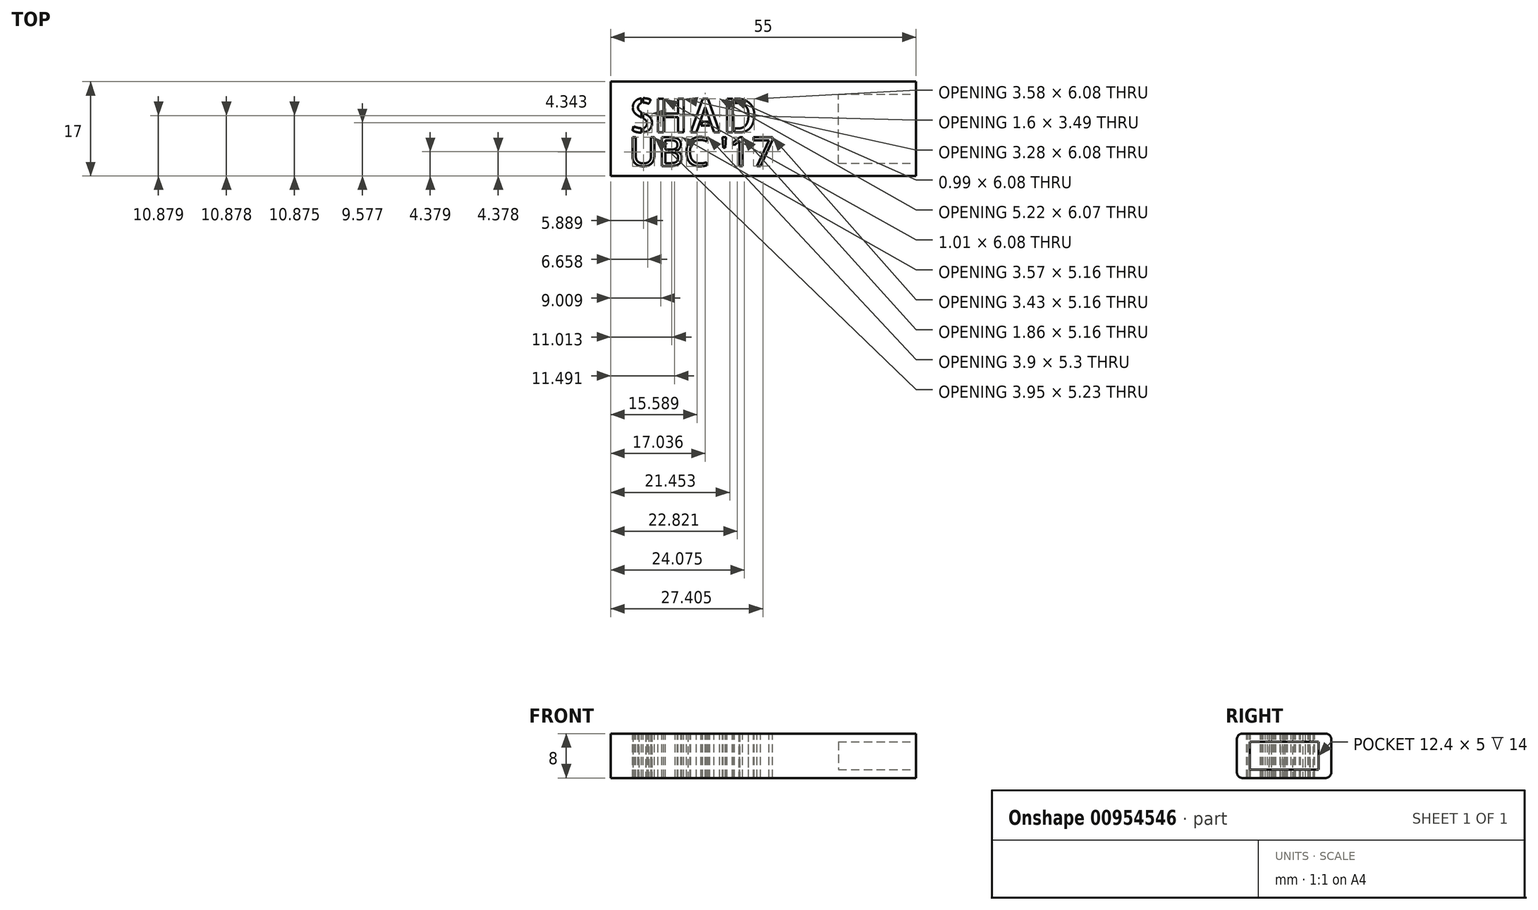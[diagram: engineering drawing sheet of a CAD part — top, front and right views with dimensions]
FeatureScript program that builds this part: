
annotation { "Feature Type Name" : "Feature", "Feature Type Description" : "" }
export const myFeature = defineFeature(function(context is Context, id is Id, definition is map)
    precondition{}
    {
        {
            var Q0;
            Q0=qCreatedBy(makeId("Front.planeOp"),FACE);
            var sketch = newSketch(context, id + "F0", { "sketchPlane" : qUnion([Q0])});
            skLineSegment(sketch, "E0.bottom", {"start": v(-7.5, 4) * mm, "end": v(7.5, 4) * mm});
            skLineSegment(sketch, "E0.top", {"start": v(-7.5, -4) * mm, "end": v(7.5, -4) * mm});
            skLineSegment(sketch, "E0.left", {"start": v(-8.5, 3) * mm, "end": v(-8.5, -3) * mm});
            skLineSegment(sketch, "E0.right", {"start": v(8.5, 3) * mm, "end": v(8.5, -3) * mm});
            skPoint(sketch, "E1.visualSharp", {"position": v(-8.5, 4) * mm});
            skArc(sketch, "E1.filletArc", {"start": v(-7.5, 4) * mm, "mid": v(-8.2, 3.7) * mm, "end": v(-8.5, 3) * mm});
            skPoint(sketch, "E2.visualSharp", {"position": v(8.5, 4) * mm});
            skArc(sketch, "E2.filletArc", {"start": v(8.5, 3) * mm, "mid": v(8.2, 3.7) * mm, "end": v(7.5, 4) * mm});
            skPoint(sketch, "E3.visualSharp", {"position": v(8.5, -4) * mm});
            skArc(sketch, "E3.filletArc", {"start": v(7.5, -4) * mm, "mid": v(8.2, -3.7) * mm, "end": v(8.5, -3) * mm});
            skPoint(sketch, "E4.visualSharp", {"position": v(-8.5, -4) * mm});
            skArc(sketch, "E4.filletArc", {"start": v(-8.5, -3) * mm, "mid": v(-8.2, -3.7) * mm, "end": v(-7.5, -4) * mm});
            skSolve(sketch);
        }
        {
            var Q0;
            Q0 = qSketchRegion(id + "F0", true);
            extrude(context, id + "F1", {"entities" : qUnion([Q0]), "depth" : 55 * mm, "offsetDistance" : 25 * mm});
        }
        {
            var Q0;
            Q0=makeQuery(id+"F1.opExtrude","CAP_FACE",FACE,{"disambiguationData":[OSD([sQuery(id+"F0.wireOp",EDGE,"E0.bottom"),sQuery(id+"F0.wireOp",EDGE,"E0.top"),sQuery(id+"F0.wireOp",EDGE,"E0.left"),sQuery(id+"F0.wireOp",EDGE,"E0.right"),sQuery(id+"F0.wireOp",EDGE,"E1.filletArc"),sQuery(id+"F0.wireOp",EDGE,"E2.filletArc"),sQuery(id+"F0.wireOp",EDGE,"E3.filletArc"),sQuery(id+"F0.wireOp",EDGE,"E4.filletArc")])],"isStart":false});
            var sketch = newSketch(context, id + "F2", { "sketchPlane" : qUnion([Q0])});
            skLineSegment(sketch, "E5.bottom", {"start": v(-6.2, 2.5) * mm, "end": v(6.2, 2.5) * mm});
            skLineSegment(sketch, "E5.top", {"start": v(-6.2, -2.5) * mm, "end": v(6.2, -2.5) * mm});
            skLineSegment(sketch, "E5.left", {"start": v(-6.2, 2.5) * mm, "end": v(-6.2, -2.5) * mm});
            skLineSegment(sketch, "E5.right", {"start": v(6.2, 2.5) * mm, "end": v(6.2, -2.5) * mm});
            skSolve(sketch);
        }
        {
            var Q0;
            Q0=makeQuery(id+"F2.imprint","IMPRINT",FACE,{"disambiguationData":[TD([[makeQuery(id+"F2.imprint","IMPRINT",EDGE,{"derivedFrom":sQuery(id+"F2.wireOp",EDGE,"E5.bottom")}),-1.0]])]});
            extrude(context, id + "F3", {"entities" : qUnion([Q0]), "operationType" : NewBodyOperationType.REMOVE, "oppositeDirection" : true, "depth" : 14 * mm, "offsetDistance" : 25 * mm});
        }
        {
            var Q0;
            Q0=makeQuery(id+"F1.opExtrude","SWEPT_BODY",BODY,{"disambiguationData":[OSD([sQuery(id+"F0.wireOp",EDGE,"E0.bottom"),sQuery(id+"F0.wireOp",EDGE,"E0.top"),sQuery(id+"F0.wireOp",EDGE,"E0.left"),sQuery(id+"F0.wireOp",EDGE,"E0.right"),sQuery(id+"F0.wireOp",EDGE,"E1.filletArc"),sQuery(id+"F0.wireOp",EDGE,"E2.filletArc"),sQuery(id+"F0.wireOp",EDGE,"E3.filletArc"),sQuery(id+"F0.wireOp",EDGE,"E4.filletArc")])]});
            var Q1;
            Q1=makeQuery(id+"F1.opExtrude","CAP_EDGE",EDGE,{"disambiguationData":[OSD([sQuery(id+"F0.wireOp",EDGE,"E0.left")])],"isStart":true});
            transform(context, id + "F4", {"entities" : qUnion([Q0]), "transformType" : TransformType.ROTATION, "transformAxis" : qUnion([Q1]), "angle" : 270 * degree, "makeCopy" : false});
        }
        {
            var Q0;
            Q0=makeQuery(id+"F1.opExtrude","SWEPT_FACE",FACE,{"disambiguationData":[OSD([sQuery(id+"F0.wireOp",EDGE,"E0.bottom")])]});
            var sketch = newSketch(context, id + "F5", { "sketchPlane" : qUnion([Q0])});
            skText(sketch, "E6", { "text": "SHAD", "fontName": "AllertaStencil-Regular.ttf"});
            const initialGuessF5  = {"E6": [-0.00524, 0.00784, 1, 0, 0.00608]};
            skSetInitialGuess(sketch, initialGuessF5);
            skSolve(sketch);
        }
        {
            var Q0;
            Q0 = qSketchRegion(id + "F5", true);
            extrude(context, id + "F6", {"entities" : qUnion([Q0]), "operationType" : NewBodyOperationType.REMOVE, "oppositeDirection" : true, "depth" : 25 * mm, "offsetDistance" : 25 * mm});
        }
        {
            var Q0;
            Q0=makeQuery(id+"F1.opExtrude","SWEPT_FACE",FACE,{"disambiguationData":[OSD([sQuery(id+"F0.wireOp",EDGE,"E0.bottom")])]});
            var sketch = newSketch(context, id + "F7", { "sketchPlane" : qUnion([Q0])});
            skPoint(sketch, "E7.firstSnap0", {"position": v(19, 1) * mm});
            skSolve(sketch);
        }
        {
            var Q0;
            Q0 = qSketchRegion(id + "F5", true);
            extrude(context, id + "F8", {"entities" : qUnion([Q0]), "operationType" : NewBodyOperationType.REMOVE, "oppositeDirection" : true, "depth" : 25 * mm, "offsetDistance" : 25 * mm});
        }
        {
            var Q0;
            {var subQ0=sQuery(id+"F0.wireOp",EDGE,"E0.bottom");Q0=makeQuery(id+"F7.imprint","IMPRINT",FACE,{"disambiguationData":[TD([[makeQuery(id+"F7.imprint","IMPRINT",EDGE,{"derivedFrom":makeQuery(id+"F1.opExtrude","CAP_EDGE",EDGE,{"disambiguationData":[OSD([subQ0])],"isStart":true})}),-1.0]])]});}
            var sketch = newSketch(context, id + "F9", { "sketchPlane" : qUnion([Q0])});
            skText(sketch, "E8", { "text": "UBC \'17", "fontName": "OpenSans-Regular.ttf"});
            const initialGuessF9  = {"E8": [-0.00524, 0.0018, 1, 0, 0.0052]};
            skSetInitialGuess(sketch, initialGuessF9);
            skSolve(sketch);
        }
        {
            var Q0;
            Q0 = qSketchRegion(id + "F9", true);
            extrude(context, id + "F10", {"entities" : qUnion([Q0]), "operationType" : NewBodyOperationType.REMOVE, "oppositeDirection" : true, "depth" : 25 * mm, "offsetDistance" : 25 * mm});
        }
    });
